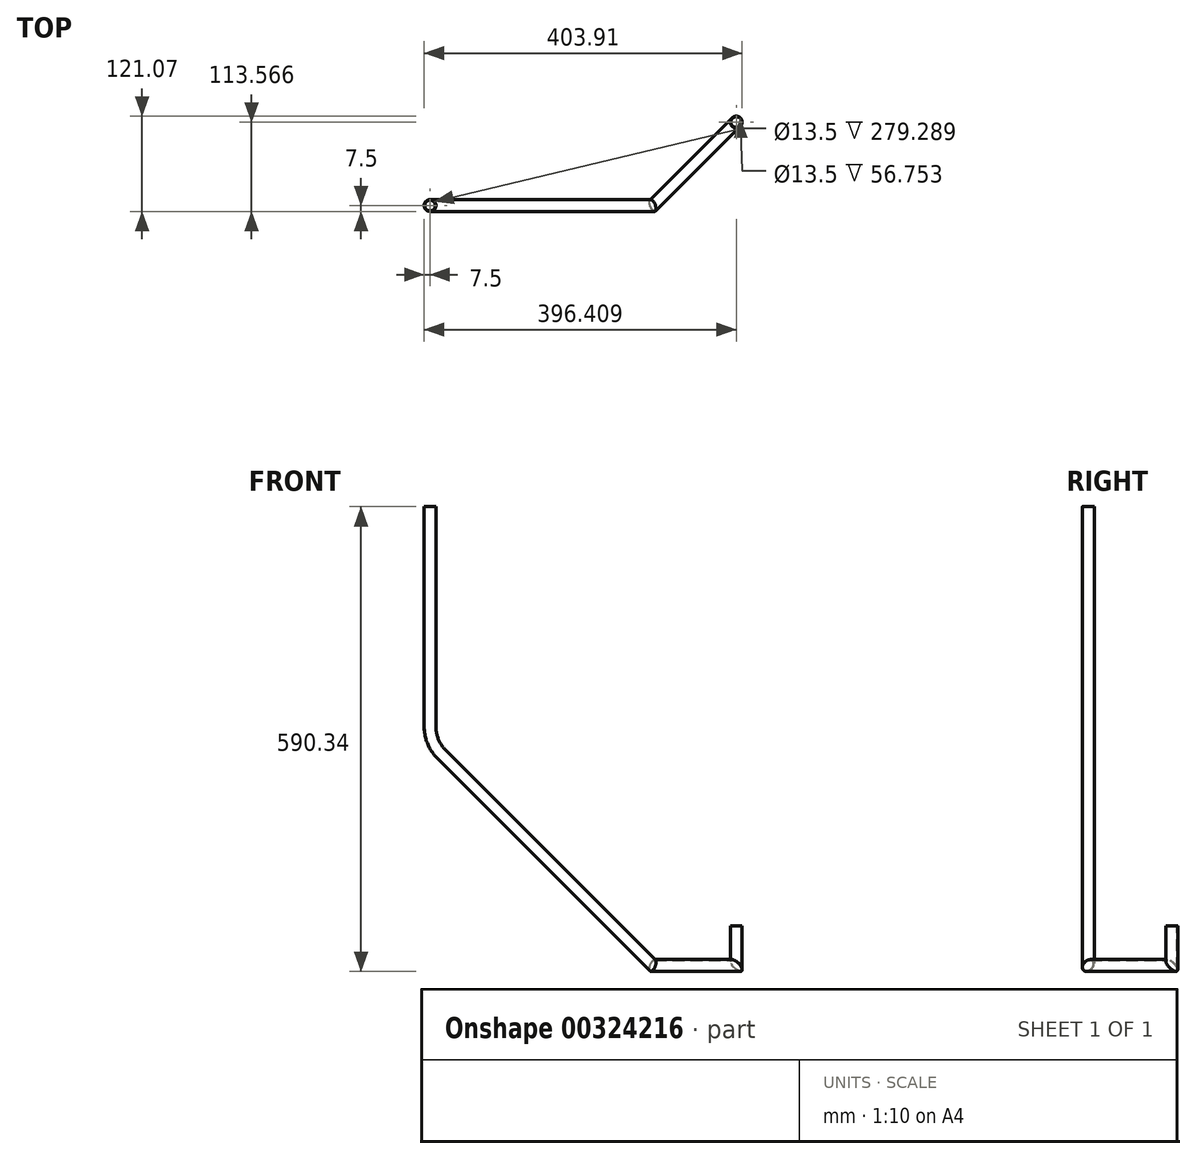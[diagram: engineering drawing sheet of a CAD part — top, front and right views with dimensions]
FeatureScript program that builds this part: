
annotation { "Feature Type Name" : "Feature", "Feature Type Description" : "" }
export const myFeature = defineFeature(function(context is Context, id is Id, definition is map)
    precondition{}
    {
        {
            var Q0;
            Q0=qCreatedBy(makeId("Front.planeOp"),FACE);
            var sketch = newSketch(context, id + "F0", { "sketchPlane" : qUnion([Q0])});
            skLineSegment(sketch, "E0", {"start": v(0, 0) * mm, "end": v(0, -279.29) * mm});
            skLineSegment(sketch, "E1", {"start": v(14.64, -314.64) * mm, "end": v(282.84, -582.84) * mm});
            skPoint(sketch, "E2.visualSharp", {"position": v(0, -300) * mm});
            skArc(sketch, "E2.filletArc", {"start": v(0, -279.29) * mm, "mid": v(3.8, -298.42) * mm, "end": v(14.64, -314.64) * mm});
            skSolve(sketch);
        }
        {
            var Q0;
            Q0=qCreatedBy(makeId("Top.planeOp"),FACE);
            var Q1;
            Q1=sQuery(id+"F0.wireOp",VERTEX,"E1.end");
            cPlane(context, id + "F1", {"entities" : qUnion([Q0, Q1]), "cplaneType" : CPlaneType.PLANE_POINT, "offset" : 25 * mm, "width" : 150 * mm, "height" : 150 * mm});
        }
        {
            var Q0;
            Q0=qCreatedBy(id+"F1.planeOp",FACE);
            var sketch = newSketch(context, id + "F2", { "sketchPlane" : qUnion([Q0])});
            skPoint(sketch, "E3.0", {"position": v(282.84, 0) * mm});
            skLineSegment(sketch, "E4", {"start": v(282.84, 0) * mm, "end": v(388.9, 106.07) * mm});
            skSolve(sketch);
        }
        {
            var Q0;
            Q0=qCreatedBy(makeId("Front.planeOp"),FACE);
            var Q1;
            Q1=sQuery(id+"F2.wireOp",VERTEX,"E4.end");
            cPlane(context, id + "F3", {"entities" : qUnion([Q0, Q1]), "cplaneType" : CPlaneType.PLANE_POINT, "offset" : 25 * mm, "width" : 150 * mm, "height" : 150 * mm});
        }
        {
            var Q0;
            Q0=qCreatedBy(id+"F3.planeOp",FACE);
            var sketch = newSketch(context, id + "F4", { "sketchPlane" : qUnion([Q0])});
            skPoint(sketch, "E5.0", {"position": v(388.9, -582.84) * mm});
            skLineSegment(sketch, "E6", {"start": v(388.9, -582.84) * mm, "end": v(388.9, -532.84) * mm});
            skSolve(sketch);
        }
        {
            var Q0;
            Q0=qCreatedBy(makeId("Top.planeOp"),FACE);
            var sketch = newSketch(context, id + "F5", { "sketchPlane" : qUnion([Q0])});
            skCircle(sketch, "E7", {"center": v(0, 0) * mm, "radius": 6.75 * mm});
            skCircle(sketch, "E8", {"center": v(0, 0) * mm, "radius": 7.5 * mm});
            skSolve(sketch);
        }
        {
            var Q0;
            Q0=makeQuery(id+"F5.imprint","IMPRINT",FACE,{"disambiguationData":[TD([[makeQuery(id+"F5.imprint","IMPRINT",EDGE,{"derivedFrom":sQuery(id+"F5.wireOp",EDGE,"E7")}),-1.0]])]});
            var Q1;
            Q1=sQuery(id+"F0.wireOp",EDGE,"E0");
            var Q2;
            Q2=sQuery(id+"F0.wireOp",EDGE,"E1");
            var Q3;
            Q3=sQuery(id+"F2.wireOp",EDGE,"E4");
            var Q4;
            Q4=sQuery(id+"F4.wireOp",EDGE,"E6");
            var Q5;
            Q5=sQuery(id+"F0.wireOp",EDGE,"E2.filletArc");
            sweep(context, id + "F6", {"profiles" : qUnion([Q0]), "path" : qUnion([Q1, Q2, Q3, Q4, Q5])});
        }
    });
